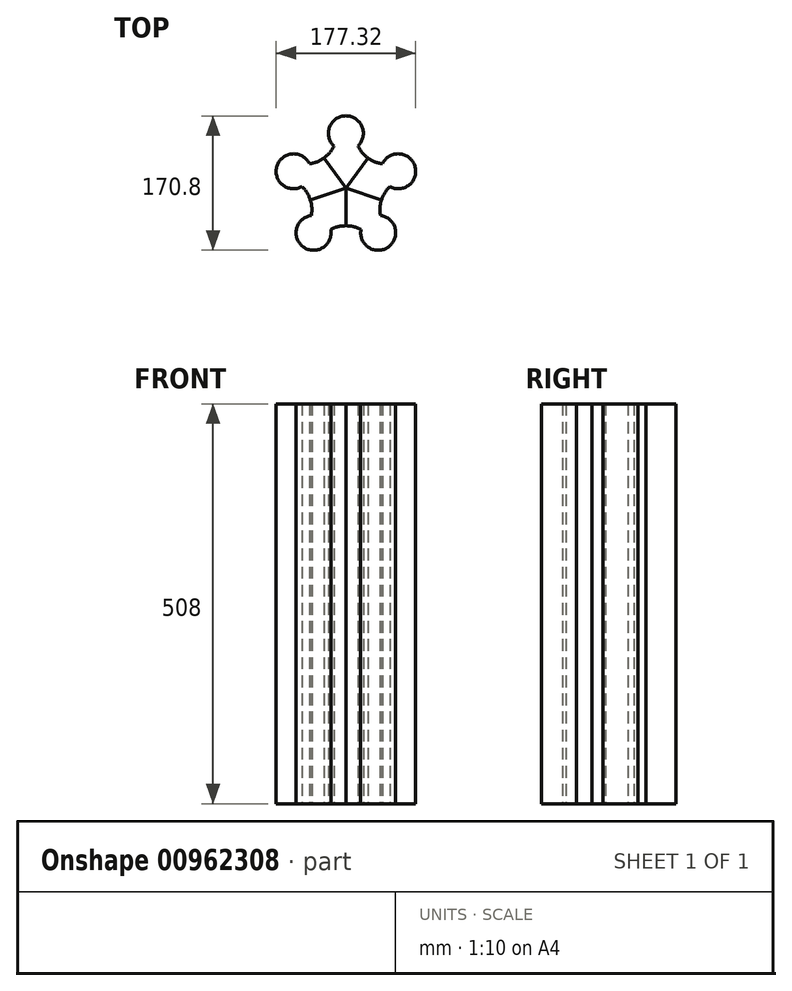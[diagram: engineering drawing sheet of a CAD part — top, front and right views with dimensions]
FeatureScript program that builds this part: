
annotation { "Feature Type Name" : "Feature", "Feature Type Description" : "" }
export const myFeature = defineFeature(function(context is Context, id is Id, definition is map)
    precondition{}
    {
        {
            var Q0;
            Q0=qCreatedBy(makeId("Top.planeOp"),FACE);
            var sketch = newSketch(context, id + "F0", { "sketchPlane" : qUnion([Q0])});
            skLineSegment(sketch, "E0", {"start": v(0, 0) * mm, "end": v(28, 38.53) * mm});
            skLineSegment(sketch, "E1", {"start": v(0, 0) * mm, "end": v(0, 69.85) * mm, "construction": true});
            skArc(sketch, "E2", {"start": v(15.27, 53.7) * mm, "mid": v(0, 92.08) * mm, "end": v(-15.27, 53.7) * mm});
            skArc(sketch, "E3", {"start": v(15.27, 53.7) * mm, "mid": v(20.63, 45.27) * mm, "end": v(28, 38.53) * mm});
            skArc(sketch, "E4.MirrorCS", {"start": v(-15.27, 53.7) * mm, "mid": v(-20.63, 45.27) * mm, "end": v(-28, 38.53) * mm});
            skLineSegment(sketch, "E5.MirrorCS", {"start": v(0, 0) * mm, "end": v(-28, 38.53) * mm});
            skSolve(sketch);
        }
        {
            var Q0;
            Q0=makeQuery(id+"F0.imprint","IMPRINT",FACE,{"disambiguationData":[TD([[makeQuery(id+"F0.imprint","IMPRINT",EDGE,{"derivedFrom":sQuery(id+"F0.wireOp",EDGE,"E0")}),1.0]])]});
            extrude(context, id + "F1", {"entities" : qUnion([Q0]), "depth" : 508 * mm, "offsetDistance" : 25.4 * mm});
        }
        {
            var Q0;
            Q0=qCreatedBy(makeId("Front.planeOp"),FACE);
            var sketch = newSketch(context, id + "F2", { "sketchPlane" : qUnion([Q0])});
            skLineSegment(sketch, "E6", {"start": v(0, 0) * mm, "end": v(0, 558.4) * mm, "construction": true});
            skSolve(sketch);
        }
        {
            var Q0;
            Q0=makeQuery(id+"F1.opExtrude","SWEPT_BODY",BODY,{"disambiguationData":[OSD([sQuery(id+"F0.wireOp",EDGE,"E0"),sQuery(id+"F0.wireOp",EDGE,"8db9f01e-8408-4349-ad31-d6c7c21c9eac0.MirrorCS"),sQuery(id+"F0.wireOp",EDGE,"xR015LW3-Eimr-QLji-nUAl-eW5IwXewGvRT"),sQuery(id+"F0.wireOp",EDGE,"E2"),sQuery(id+"F0.wireOp",EDGE,"9a391e75-2481-463a-8564-2c1e0ce7a5fc.trimOffspring"),sQuery(id+"F0.wireOp",EDGE,"b2da30bb-1da6-42bc-8d7a-e9cc3f93dfc5.filletArc"),sQuery(id+"F0.wireOp",EDGE,"60542cd6-58f5-437a-aa74-e49b5cfdf1c7.filletArc")])]});
            var Q1;
            Q1=sQuery(id+"F2.wireOp",EDGE,"E6");
            circularPattern(context, id + "F3", {"entities" : qUnion([Q0]), "axis" : qUnion([Q1]), "angle" : 360 * degree, "instanceCount" : 5, "equalSpace" : true});
        }
    });
